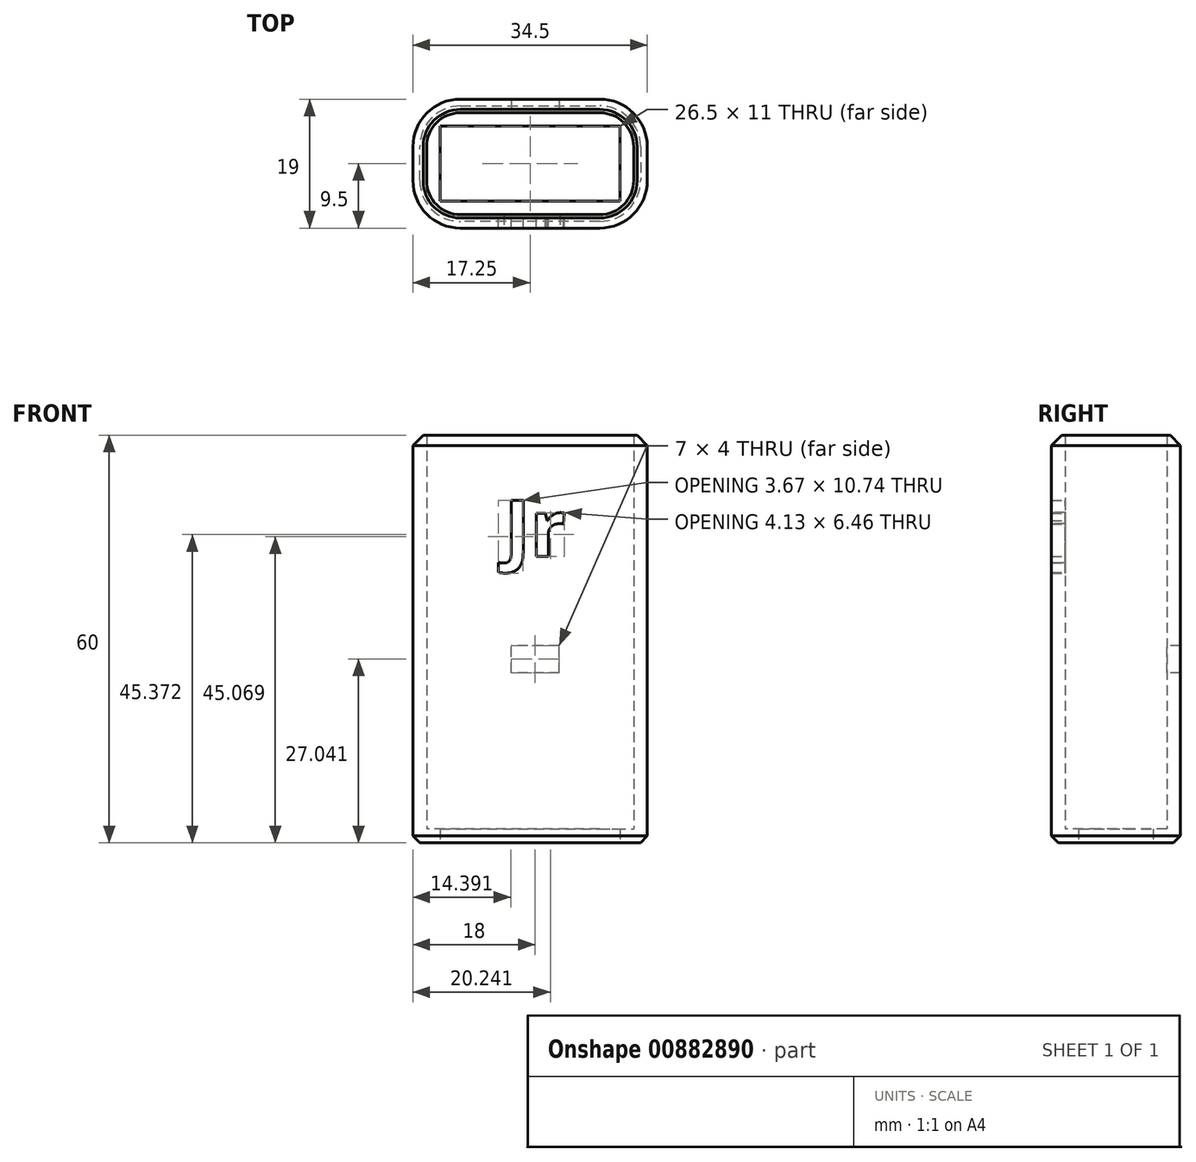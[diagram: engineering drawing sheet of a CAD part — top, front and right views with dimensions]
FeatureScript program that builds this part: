
annotation { "Feature Type Name" : "Feature", "Feature Type Description" : "" }
export const myFeature = defineFeature(function(context is Context, id is Id, definition is map)
    precondition{}
    {
        {
            var Q0;
            Q0=qCreatedBy(makeId("Top.planeOp"),FACE);
            var sketch = newSketch(context, id + "F0", { "sketchPlane" : qUnion([Q0])});
            skLineSegment(sketch, "E0.bottom", {"start": v(5, 0) * mm, "end": v(25.5, 0) * mm});
            skLineSegment(sketch, "E0.top", {"start": v(5, 15) * mm, "end": v(25.5, 15) * mm});
            skLineSegment(sketch, "E0.left", {"start": v(0, 5) * mm, "end": v(0, 10) * mm});
            skLineSegment(sketch, "E0.right", {"start": v(30.5, 5) * mm, "end": v(30.5, 10) * mm});
            skPoint(sketch, "E1.visualSharp", {"position": v(0, 15) * mm});
            skArc(sketch, "E1.filletArc", {"start": v(5, 15) * mm, "mid": v(1.46, 13.54) * mm, "end": v(0, 10) * mm});
            skPoint(sketch, "E2.visualSharp", {"position": v(0, 0) * mm});
            skArc(sketch, "E2.filletArc", {"start": v(0, 5) * mm, "mid": v(1.46, 1.46) * mm, "end": v(5, 0) * mm});
            skPoint(sketch, "E3.visualSharp", {"position": v(30.5, 15) * mm});
            skArc(sketch, "E3.filletArc", {"start": v(30.5, 10) * mm, "mid": v(29.04, 13.54) * mm, "end": v(25.5, 15) * mm});
            skPoint(sketch, "E4.visualSharp", {"position": v(30.5, 0) * mm});
            skArc(sketch, "E4.filletArc", {"start": v(25.5, 0) * mm, "mid": v(29.04, 1.46) * mm, "end": v(30.5, 5) * mm});
            skArc(sketch, "E5.0", {"start": v(5, 17) * mm, "mid": v(0.05, 14.95) * mm, "end": v(-2, 10) * mm});
            skLineSegment(sketch, "E5.1", {"start": v(-2, 5) * mm, "end": v(-2, 10) * mm});
            skLineSegment(sketch, "E5.2", {"start": v(5, 17) * mm, "end": v(25.5, 17) * mm});
            skArc(sketch, "E5.3", {"start": v(-2, 5) * mm, "mid": v(0.05, 0.05) * mm, "end": v(5, -2) * mm});
            skArc(sketch, "E5.4", {"start": v(32.5, 10) * mm, "mid": v(30.45, 14.95) * mm, "end": v(25.5, 17) * mm});
            skLineSegment(sketch, "E5.5", {"start": v(32.5, 5) * mm, "end": v(32.5, 10) * mm});
            skArc(sketch, "E5.6", {"start": v(25.5, -2) * mm, "mid": v(30.45, 0.05) * mm, "end": v(32.5, 5) * mm});
            skLineSegment(sketch, "E5.7", {"start": v(5, -2) * mm, "end": v(25.5, -2) * mm});
            skLineSegment(sketch, "E6.0", {"start": v(2, 13) * mm, "end": v(28.5, 13) * mm});
            skLineSegment(sketch, "E6.1", {"start": v(2, 2) * mm, "end": v(2, 13) * mm});
            skLineSegment(sketch, "E6.2", {"start": v(2, 2) * mm, "end": v(28.5, 2) * mm});
            skLineSegment(sketch, "E6.3", {"start": v(28.5, 2) * mm, "end": v(28.5, 13) * mm});
            skSolve(sketch);
        }
        {
            var Q0;
            Q0=makeQuery(id+"F0.imprint","IMPRINT",FACE,{"disambiguationData":[TD([[makeQuery(id+"F0.imprint","IMPRINT",EDGE,{"derivedFrom":sQuery(id+"F0.wireOp",EDGE,"E0.bottom")}),1.0]])]});
            var Q1;
            Q1=makeQuery(id+"F0.imprint","IMPRINT",FACE,{"disambiguationData":[TD([[makeQuery(id+"F0.imprint","IMPRINT",EDGE,{"derivedFrom":sQuery(id+"F0.wireOp",EDGE,"E0.bottom")}),-1.0]])]});
            extrude(context, id + "F1", {"entities" : qUnion([Q0, Q1]), "depth" : 2 * mm, "offsetDistance" : 25 * mm});
        }
        {
            var Q0;
            Q0=makeQuery(id+"F0.imprint","IMPRINT",FACE,{"disambiguationData":[TD([[makeQuery(id+"F0.imprint","IMPRINT",EDGE,{"derivedFrom":sQuery(id+"F0.wireOp",EDGE,"E0.bottom")}),-1.0]])]});
            extrude(context, id + "F2", {"entities" : qUnion([Q0]), "operationType" : NewBodyOperationType.ADD, "depth" : 60 * mm, "offsetDistance" : 25 * mm});
        }
        {
            var Q0;
            Q0=qCreatedBy(makeId("Front.planeOp"),FACE);
            var sketch = newSketch(context, id + "F3", { "sketchPlane" : qUnion([Q0])});
            skLineSegment(sketch, "E7.bottom", {"start": v(12.5, 29.04) * mm, "end": v(19.5, 29.04) * mm});
            skLineSegment(sketch, "E7.top", {"start": v(12.5, 25.04) * mm, "end": v(19.5, 25.04) * mm});
            skLineSegment(sketch, "E7.left", {"start": v(12.5, 29.04) * mm, "end": v(12.5, 25.04) * mm});
            skLineSegment(sketch, "E7.right", {"start": v(19.5, 29.04) * mm, "end": v(19.5, 25.04) * mm});
            skSolve(sketch);
        }
        {
            var Q0;
            Q0=makeQuery(id+"F3.imprint","IMPRINT",FACE,{"disambiguationData":[TD([[makeQuery(id+"F3.imprint","IMPRINT",EDGE,{"derivedFrom":sQuery(id+"F3.wireOp",EDGE,"E7.bottom")}),-1.0]])]});
            extrude(context, id + "F4", {"entities" : qUnion([Q0]), "operationType" : NewBodyOperationType.REMOVE, "oppositeDirection" : true, "depth" : 25 * mm, "offsetDistance" : 25 * mm});
        }
        {
            var Q0;
            Q0=qCreatedBy(makeId("Front.planeOp"),FACE);
            var sketch = newSketch(context, id + "F5", { "sketchPlane" : qUnion([Q0])});
            skText(sketch, "E8", { "text": "Jr", "fontName": "OpenSans-Bold.ttf"});
            const initialGuessF5  = {"E8": [0.01142, 0.04214, 1, 0, 0.00837]};
            skSetInitialGuess(sketch, initialGuessF5);
            skSolve(sketch);
        }
        {
            var Q0;
            Q0=qSketchRegion(id+"F5",true);
            extrude(context, id + "F6", {"entities" : qUnion([Q0]), "operationType" : NewBodyOperationType.REMOVE, "depth" : 25 * mm, "offsetDistance" : 25 * mm});
        }
        {
            var Q0;
            Q0=makeQuery(id+"F1.opExtrude","CAP_EDGE",EDGE,{"disambiguationData":[OSD([sQuery(id+"F0.wireOp",EDGE,"E5.7")])],"isStart":true});
            var Q1;
            Q1=makeQuery(id+"F1.opExtrude","CAP_EDGE",EDGE,{"disambiguationData":[OSD([sQuery(id+"F0.wireOp",EDGE,"E5.3")])],"isStart":true});
            var Q2;
            Q2=makeQuery(id+"F1.opExtrude","CAP_EDGE",EDGE,{"disambiguationData":[OSD([sQuery(id+"F0.wireOp",EDGE,"E5.1")])],"isStart":true});
            var Q3;
            Q3=makeQuery(id+"F1.opExtrude","CAP_EDGE",EDGE,{"disambiguationData":[OSD([sQuery(id+"F0.wireOp",EDGE,"E5.0")])],"isStart":true});
            var Q4;
            Q4=makeQuery(id+"F1.opExtrude","CAP_EDGE",EDGE,{"disambiguationData":[OSD([sQuery(id+"F0.wireOp",EDGE,"E5.2")])],"isStart":true});
            var Q5;
            Q5=makeQuery(id+"F1.opExtrude","CAP_EDGE",EDGE,{"disambiguationData":[OSD([sQuery(id+"F0.wireOp",EDGE,"E5.4")])],"isStart":true});
            var Q6;
            Q6=makeQuery(id+"F1.opExtrude","CAP_EDGE",EDGE,{"disambiguationData":[OSD([sQuery(id+"F0.wireOp",EDGE,"E5.5")])],"isStart":true});
            var Q7;
            Q7=makeQuery(id+"F1.opExtrude","CAP_EDGE",EDGE,{"disambiguationData":[OSD([sQuery(id+"F0.wireOp",EDGE,"E5.6")])],"isStart":true});
            chamfer(context, id + "F7", {"entities" : qUnion([Q0, Q1, Q2, Q3, Q4, Q5, Q6, Q7]), "width" : 1 * mm, "tangentPropagation" : true});
        }
        {
            var Q0;
            Q0=makeQuery(id+"F2.opExtrude","CAP_EDGE",EDGE,{"disambiguationData":[OSD([sQuery(id+"F0.wireOp",EDGE,"E5.7")])],"isStart":false});
            var Q1;
            Q1=makeQuery(id+"F2.opExtrude","CAP_EDGE",EDGE,{"disambiguationData":[OSD([sQuery(id+"F0.wireOp",EDGE,"E5.6")])],"isStart":false});
            var Q2;
            Q2=makeQuery(id+"F2.opExtrude","CAP_EDGE",EDGE,{"disambiguationData":[OSD([sQuery(id+"F0.wireOp",EDGE,"E5.5")])],"isStart":false});
            var Q3;
            Q3=makeQuery(id+"F2.opExtrude","CAP_EDGE",EDGE,{"disambiguationData":[OSD([sQuery(id+"F0.wireOp",EDGE,"E5.4")])],"isStart":false});
            var Q4;
            Q4=makeQuery(id+"F2.opExtrude","CAP_EDGE",EDGE,{"disambiguationData":[OSD([sQuery(id+"F0.wireOp",EDGE,"E5.2")])],"isStart":false});
            var Q5;
            Q5=makeQuery(id+"F2.opExtrude","CAP_EDGE",EDGE,{"disambiguationData":[OSD([sQuery(id+"F0.wireOp",EDGE,"E5.0")])],"isStart":false});
            var Q6;
            Q6=makeQuery(id+"F2.opExtrude","CAP_EDGE",EDGE,{"disambiguationData":[OSD([sQuery(id+"F0.wireOp",EDGE,"E5.1")])],"isStart":false});
            var Q7;
            Q7=makeQuery(id+"F2.opExtrude","CAP_EDGE",EDGE,{"disambiguationData":[OSD([sQuery(id+"F0.wireOp",EDGE,"E5.3")])],"isStart":false});
            chamfer(context, id + "F8", {"entities" : qUnion([Q0, Q1, Q2, Q3, Q4, Q5, Q6, Q7]), "width" : 1.5 * mm, "tangentPropagation" : true});
        }
    });
